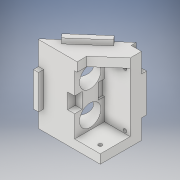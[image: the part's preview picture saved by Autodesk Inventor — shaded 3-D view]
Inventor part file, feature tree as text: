
AUTODESK INVENTOR PART (.ipt)
format: ipt  version: 2019 (Build 230136000, 136)  size: 287,232 bytes
history: native  units: mm
features: sketch x15, extrude x13, projected_geometry x3, hole x2, other x1
ambient origin geometry x8: Origin, YZ Plane, XZ Plane, XY Plane, X Axis, Y Axis, Z Axis, Center Point
bodies: Body1 (feature_tree)
feature tree (34):
  other  "Твердое тело1"
  extrude  "Выдавливание1"  Depth=35.0mm
  extrude  "Выдавливание2"  Depth=40.0mm
  extrude  "Выдавливание3"  Depth=30.0mm
  extrude  "Выдавливание4"  Depth=4.0mm
  extrude  "Выдавливание5"  Depth=22.25mm
  extrude  "Выдавливание6"  Depth=60.0mm TaperAngle=0.0deg
  extrude  "Выдавливание7"  Depth=46.0mm
  extrude  "Выдавливание8"  Depth=2.0mm TaperAngle=0.0deg
  extrude  "Выдавливание9"  Depth=16.6mm
  extrude  "Выдавливание10"  Depth=26.0mm
  extrude  "Выдавливание11"  Depth=2.0mm TaperAngle=0.0deg
  extrude  "Выдавливание12"  Depth=5.0mm
  extrude  "Выдавливание15"  Depth=12.0mm
  hole  "Отверстие1"  [1 undecoded]
  hole  "Отверстие2"  [1 undecoded]
  sketch  "Эскиз1"
  sketch  "Эскиз2"
  sketch  "Эскиз3"
  sketch  "Эскиз4"
  sketch  "Эскиз5"
  sketch  "Эскиз6"
  sketch  "Эскиз7"
  sketch  "Эскиз8"
  projected_geometry  "Спроецированная петля1"
  sketch  "Эскиз9"
  projected_geometry  "Спроецированная петля2"
  sketch  "Эскиз10"
  projected_geometry  "Спроецированная петля3"
  sketch  "Эскиз12"
  sketch  "Эскиз13"
  sketch  "Эскиз16"
  sketch  "Эскиз17"
  sketch  "Эскиз19"
note: 2 required parameter values undecoded (feature->parameter linkage not recoverable at this tier; creation-order binding heuristic only, values carry confidence <= 0.55)
